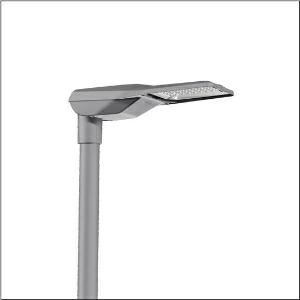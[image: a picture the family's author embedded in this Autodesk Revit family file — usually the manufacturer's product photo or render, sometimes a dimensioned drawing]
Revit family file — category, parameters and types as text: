
# Revit family: streetlight_sl_21_mini___stw1_0a_5xe6e43a08hb_5b98
name_source: partatom
category: Lighting Fixtures
units: mm (PartAtom-declared; Revit-internal decimal feet)

## family parameters
Cut with Voids When Loaded = No
Host = Face
Light Source = No
Part Type = Normal
Room Calculation Point = No
Round Connector Dimension = Use Diameter
Shared = No

## types (1)
- --- (1 x LED, 9430 lm, 66 W, 4000K)
    Apparent Load = 66 VA
    CIE Flux Codes = 38 75 98 100 100
    Color Rendering = 70
    Color Temperature = 4000K
    Default Elevation = 1800 mm
    Description = Streetlight SL 21 mini, mast luminaire, primary light control with lens, of PMMA, primary optical cover: cover, of toughened safety glass, transparent, light distribution: STW1.0a, light emission: direct distribution, primary light characteristic: asymmetric, installation type: post-top, side-entry, LED, 3G 1.5mm², High Power LED, rated luminous flux: 9.430lm, luminous efficacy: 143lm/W, light colour: 740, colour temperature: 4000K, control: overheat protection, constant luminous flux control, time-dependent luminous flux control, flexible luminous flux parameterisation, mains connection: 230..240V, AC, 50/60Hz, connection cable pre-assembled, cable length: 8,5m, wiring characteristics: H07RN-F, start of lifetime: 66W, end of service life: 69W, reduction: 30W, luminaire housing, of diecast aluminium, powder-coated, Siteco® metallic grey (DB 702S), corrosivity category C5 mid according to DIN EN ISO 12944, please order mast flange separately, inclination adjustable: 0°, 5°, 10°, 15°, sealing non-destructively replaceable, multi-level sealing system, length: 628mm, width: 235mm, height: 110mm, mast flange for spigot size: 42mm (side-entry): 5XC10008XM4, 60/48mm (side-entry/post-top): 5XC10108XM2, 76/60mm (side-entry/post-top): 5XC10108XM1, protection rating (complete): IP66, insulation class (complete): insulation class II (safety insulation), certification: CE, ENEC, ENEC+, VDE, impact resistance: IK09, permissible operating ambient temperature for outdoor applications: -40..+50°C, standard-compliant lighting for roads and squares, packaging unit: 1 piece

Light Distribution: STW1.0a
    Height = 110 mm
    Lamp = 1 x LED
    Lamp Light Flux = 9430 lm
    Lamp Power = 66 W
    Lamp count = 1
    Length = 625 mm
    Luminous efficacy = 143 lm/W
    Manufacturer = Siteco
    ModVariant = No
    Model = 5XE6E43A08HB
    Number of Poles = 1
    OnlyDefault = Yes
    Power Factor = 1
    Product Name = Streetlight SL 21 mini | STW1.0a
    Product group = mast luminaire | pylon top
    ProductGroupID = 6100
    Protection Class = Protection class II
    Protection Degree = IP 66
    RLX_Detail_Level = 1
    RLX_Emergency_Light_Flux = 0 lm
    RLX_Emergency_Type = 0
    RLX_Emergency_Type_DB = No
    RlxData = <blob elided: 92125 chars, md5=0b377194>
    Socket = socket
    Standby Power = 0 W
    System Light Flux = 9430 lm
    System Power = 66 W
    Type Comments = factory setting: luminous flux: 100 % | Output Level: 100 % | 670 mA
    Type Image = l_1003519.jpg
    URL = http://relux.com
    VarID = @adj_138759
    Voltage = 0 V
    Weight = 0.00 kg
    Width = 234 mm

## geometry (parser evidence)
native form markers: Blend x4, Sweep x10
no freeform markers — native parametric forms only
